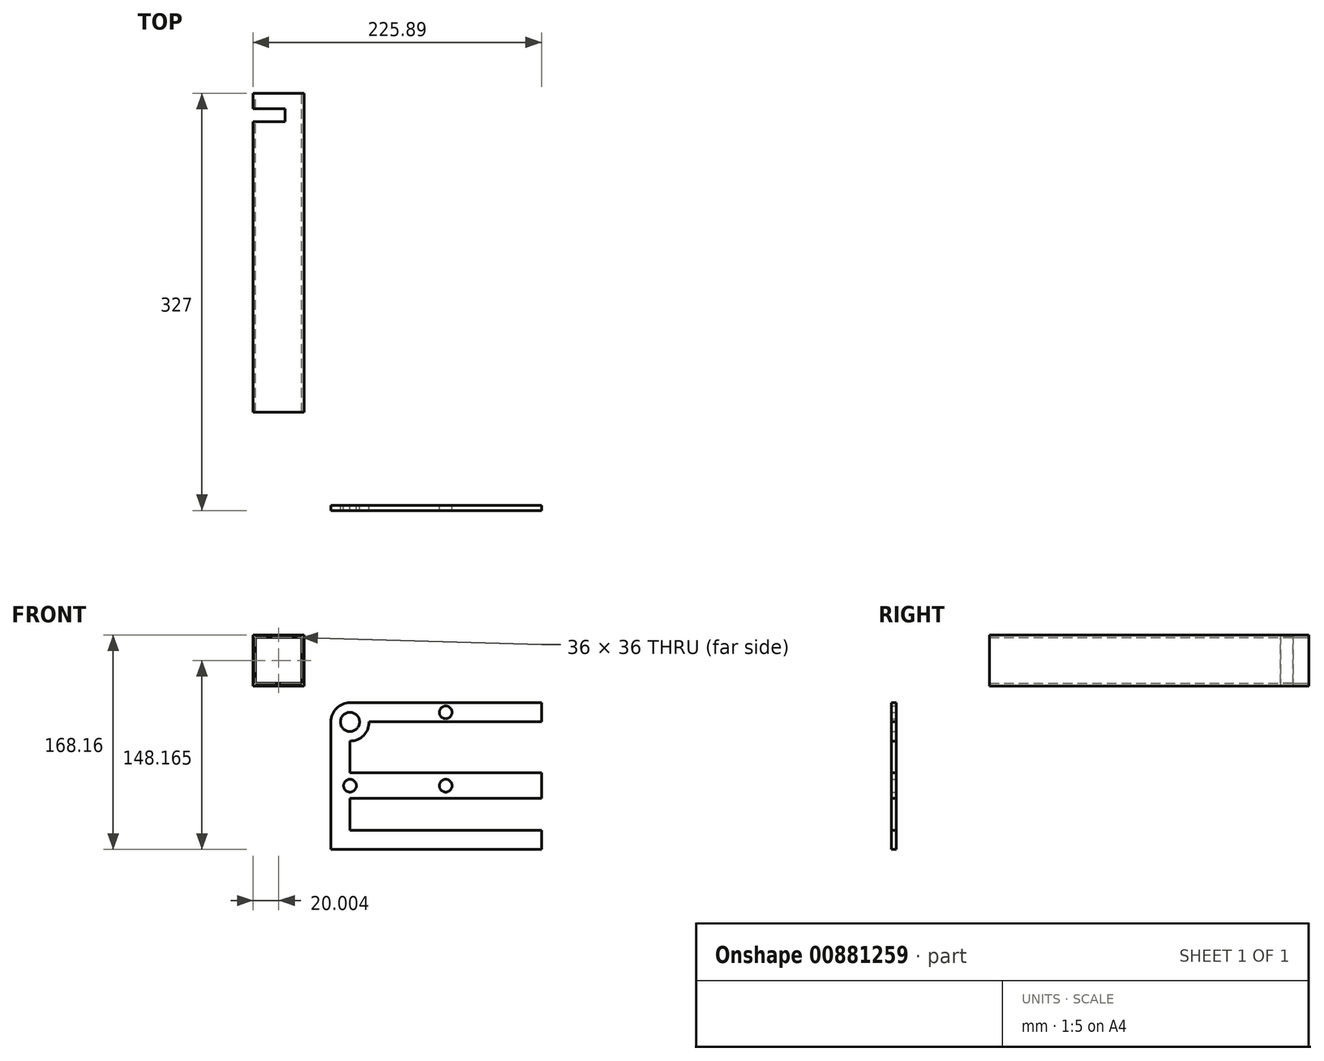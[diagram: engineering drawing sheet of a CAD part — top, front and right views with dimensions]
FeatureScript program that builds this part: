
annotation { "Feature Type Name" : "Feature", "Feature Type Description" : "" }
export const myFeature = defineFeature(function(context is Context, id is Id, definition is map)
    precondition{}
    {
        {
            assignVariable(context, id + "F0", {"name" : "Entraxe", "anyValue" : 200});
        }
        {
            var Q0;
            Q0=qCreatedBy(makeId("Front.planeOp"),FACE);
            cPlane(context, id + "F1", {"entities" : qUnion([Q0]), "cplaneType" : CPlaneType.OFFSET, "offset" : (getVariable(context, 'Entraxe')) * mm, "width" : 150 * mm, "height" : 150 * mm});
        }
        {
            var Q0;
            Q0=qCreatedBy(id+"F1.planeOp",FACE);
            var sketch = newSketch(context, id + "F2", { "sketchPlane" : qUnion([Q0])});
            skLineSegment(sketch, "E0", {"start": v(-15, -100) * mm, "end": v(-15, 0) * mm});
            skLineSegment(sketch, "E1", {"start": v(0, -60) * mm, "end": v(150, -60) * mm});
            skLineSegment(sketch, "E2", {"start": v(150, -60) * mm, "end": v(150, -40) * mm});
            skLineSegment(sketch, "E3", {"start": v(150, -40) * mm, "end": v(0, -40) * mm});
            skLineSegment(sketch, "E4", {"start": v(0, -40) * mm, "end": v(0, -15) * mm});
            skLineSegment(sketch, "E5", {"start": v(0, 15) * mm, "end": v(150, 15) * mm});
            skLineSegment(sketch, "E6", {"start": v(150, 15) * mm, "end": v(150, 0) * mm});
            skLineSegment(sketch, "E7", {"start": v(150, 0) * mm, "end": v(15, 0) * mm});
            skArc(sketch, "E8", {"start": v(-15, 0) * mm, "mid": v(-10.6, 10.6) * mm, "end": v(0, 15) * mm});
            skArc(sketch, "E9", {"start": v(0, -15) * mm, "mid": v(10.6, -10.6) * mm, "end": v(15, 0) * mm});
            skCircle(sketch, "E10", {"center": v(0, -50) * mm, "radius": 5 * mm});
            skCircle(sketch, "E11", {"center": v(0, 0) * mm, "radius": 7.5 * mm});
            skCircle(sketch, "E12", {"center": v(75, -50) * mm, "radius": 5 * mm});
            skLineSegment(sketch, "E13", {"start": v(0, -50) * mm, "end": v(75, -50) * mm, "construction": true});
            skCircle(sketch, "E14", {"center": v(75, 7.5) * mm, "radius": 5 * mm});
            skLineSegment(sketch, "E15", {"start": v(75, 7.5) * mm, "end": v(75, 0) * mm, "construction": true});
            skLineSegment(sketch, "E16", {"start": v(75, 15) * mm, "end": v(75, 7.5) * mm, "construction": true});
            skLineSegment(sketch, "E17", {"start": v(0, -60) * mm, "end": v(0, -85) * mm});
            skLineSegment(sketch, "E18", {"start": v(0, -85) * mm, "end": v(150, -85) * mm});
            skLineSegment(sketch, "E19", {"start": v(150, -85) * mm, "end": v(150, -100) * mm});
            skLineSegment(sketch, "E20", {"start": v(150, -100) * mm, "end": v(-15, -100) * mm});
            skLineSegment(sketch, "E21", {"start": v(0, -40) * mm, "end": v(0, -50) * mm, "construction": true});
            skLineSegment(sketch, "E22", {"start": v(0, -50) * mm, "end": v(0, -60) * mm, "construction": true});
            skSolve(sketch);
        }
        {
            var Q0;
            Q0=makeQuery(id+"F2.imprint","IMPRINT",FACE,{"disambiguationData":[TD([[makeQuery(id+"F2.imprint","IMPRINT",EDGE,{"derivedFrom":sQuery(id+"F2.wireOp",EDGE,"E0")}),-1.0]])]});
            extrude(context, id + "F3", {"entities" : qUnion([Q0]), "endBound" : BoundingType.SYMMETRIC, "depth" : 4 * mm, "offsetDistance" : 25 * mm});
        }
        {
            var Q0;
            Q0=qCreatedBy(makeId("Front.planeOp"),FACE);
            var sketch = newSketch(context, id + "F4", { "sketchPlane" : qUnion([Q0])});
            skLineSegment(sketch, "E23.bottom", {"start": v(-75.89, 68.16) * mm, "end": v(-35.89, 68.16) * mm});
            skLineSegment(sketch, "E23.top", {"start": v(-75.89, 28.16) * mm, "end": v(-35.89, 28.16) * mm});
            skLineSegment(sketch, "E23.left", {"start": v(-75.89, 68.16) * mm, "end": v(-75.89, 28.16) * mm});
            skLineSegment(sketch, "E23.right", {"start": v(-35.89, 68.16) * mm, "end": v(-35.89, 28.16) * mm});
            skLineSegment(sketch, "E24.bottom", {"start": v(-73.89, 66.16) * mm, "end": v(-37.89, 66.16) * mm});
            skLineSegment(sketch, "E24.top", {"start": v(-73.89, 30.16) * mm, "end": v(-37.89, 30.16) * mm});
            skLineSegment(sketch, "E24.left", {"start": v(-73.89, 66.16) * mm, "end": v(-73.89, 30.16) * mm});
            skLineSegment(sketch, "E24.right", {"start": v(-37.89, 66.16) * mm, "end": v(-37.89, 30.16) * mm});
            skLineSegment(sketch, "E25", {"start": v(-75.89, 68.16) * mm, "end": v(-35.89, 28.16) * mm, "construction": true});
            skLineSegment(sketch, "E26", {"start": v(-35.89, 68.16) * mm, "end": v(-75.89, 28.16) * mm, "construction": true});
            skSolve(sketch);
        }
        {
            var Q0;
            Q0 = qSketchRegion(id + "F4", true);
            extrude(context, id + "F5", {"entities" : qUnion([Q0]), "endBound" : BoundingType.SYMMETRIC, "depth" : 250 * mm, "offsetDistance" : 25 * mm});
        }
        {
            var Q0;
            Q0=makeQuery(id+"F5.opExtrude","SWEPT_FACE",FACE,{"disambiguationData":[OSD([sQuery(id+"F4.wireOp",EDGE,"E23.left")])]});
            var sketch = newSketch(context, id + "F6", { "sketchPlane" : qUnion([Q0])});
            skLineSegment(sketch, "E27.bottom", {"start": v(-112.8, 111.16) * mm, "end": v(-102.8, 111.16) * mm});
            skLineSegment(sketch, "E27.top", {"start": v(-112.8, 11.15) * mm, "end": v(-102.8, 11.15) * mm});
            skLineSegment(sketch, "E27.left", {"start": v(-112.8, 111.16) * mm, "end": v(-112.8, 11.15) * mm});
            skLineSegment(sketch, "E27.right", {"start": v(-102.8, 111.16) * mm, "end": v(-102.8, 11.15) * mm});
            skSolve(sketch);
        }
        {
            var Q0;
            Q0 = qSketchRegion(id + "F6", true);
            extrude(context, id + "F7", {"entities" : qUnion([Q0]), "operationType" : NewBodyOperationType.REMOVE, "oppositeDirection" : true, "depth" : 25 * mm, "offsetDistance" : 25 * mm});
        }
    });
